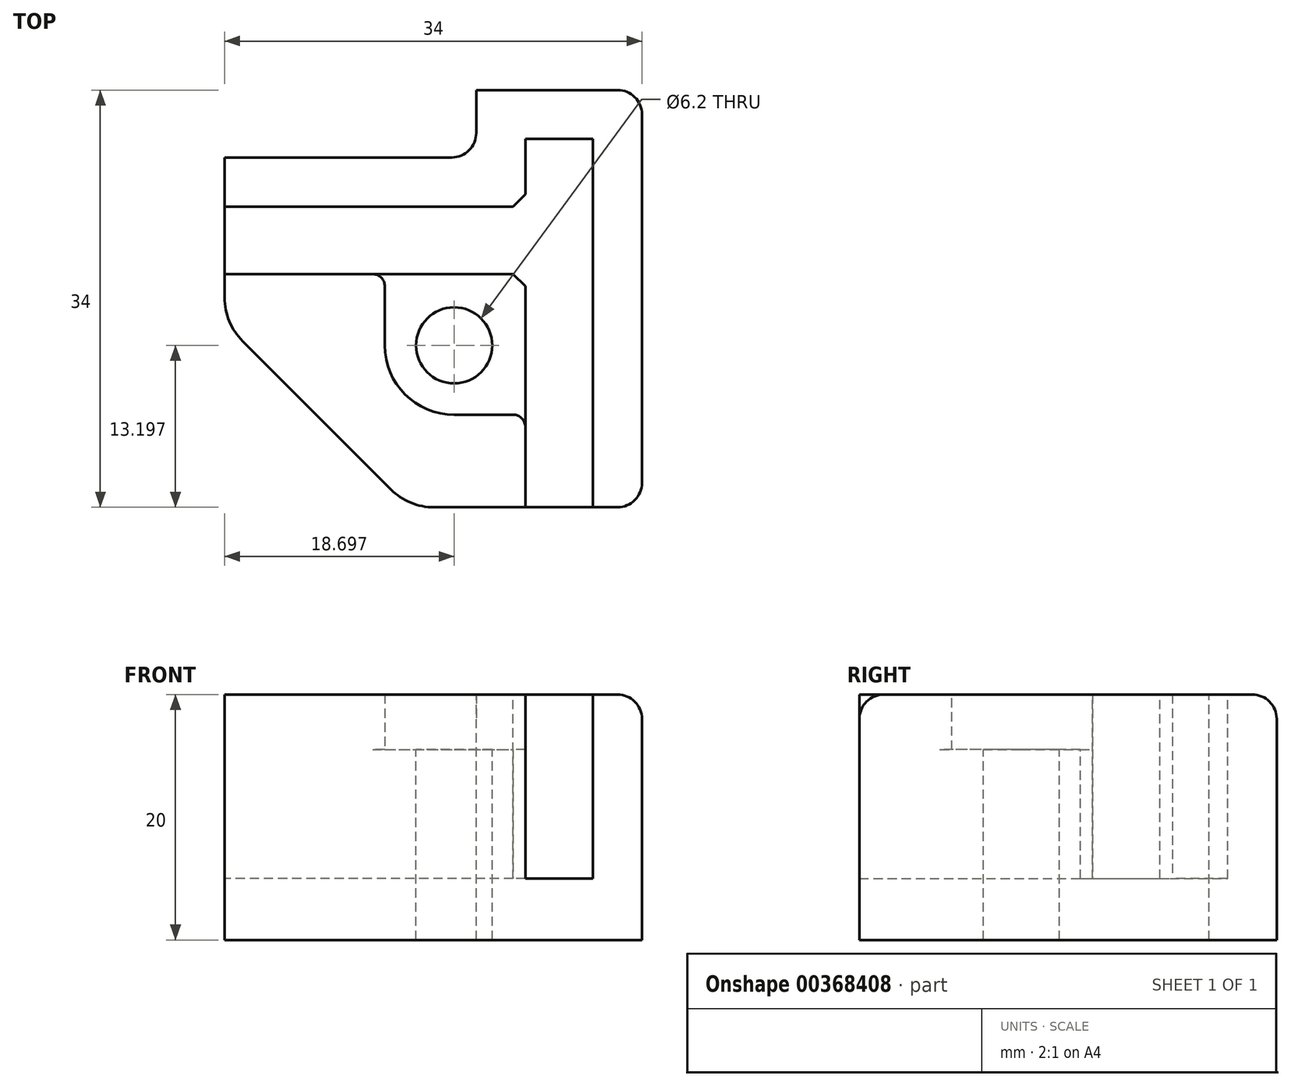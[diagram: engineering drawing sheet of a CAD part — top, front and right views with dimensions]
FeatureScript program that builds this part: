
annotation { "Feature Type Name" : "Feature", "Feature Type Description" : "" }
export const myFeature = defineFeature(function(context is Context, id is Id, definition is map)
    precondition{}
    {
        {
            var Q0;
            Q0=qCreatedBy(makeId("Top.planeOp"),FACE);
            var sketch = newSketch(context, id + "F0", { "sketchPlane" : qUnion([Q0])});
            skLineSegment(sketch, "E0.bottom", {"start": v(0, 0) * mm, "end": v(34, 0) * mm});
            skLineSegment(sketch, "E0.top", {"start": v(0, 34) * mm, "end": v(34, 34) * mm});
            skLineSegment(sketch, "E0.left", {"start": v(0, 0) * mm, "end": v(0, 34) * mm});
            skLineSegment(sketch, "E0.right", {"start": v(34, 0) * mm, "end": v(34, 34) * mm});
            skSolve(sketch);
        }
        {
            var Q0;
            Q0 = qSketchRegion(id + "F0", true);
            extrude(context, id + "F1", {"entities" : qUnion([Q0]), "depth" : 20 * mm});
        }
        {
            var Q0;
            Q0=makeQuery(id+"F1.opExtrude","CAP_FACE",FACE,{"disambiguationData":[OSD([sQuery(id+"F0.wireOp",EDGE,"E0.bottom"),sQuery(id+"F0.wireOp",EDGE,"E0.top"),sQuery(id+"F0.wireOp",EDGE,"E0.left"),sQuery(id+"F0.wireOp",EDGE,"E0.right")])],"isStart":false});
            var sketch = newSketch(context, id + "F2", { "sketchPlane" : qUnion([Q0])});
            skLineSegment(sketch, "E1", {"start": v(30, 0) * mm, "end": v(30, 30) * mm});
            skLineSegment(sketch, "E2", {"start": v(30, 30) * mm, "end": v(24.5, 30) * mm});
            skLineSegment(sketch, "E3", {"start": v(24.5, 30) * mm, "end": v(24.5, 24.5) * mm});
            skLineSegment(sketch, "E4", {"start": v(24.5, 24.5) * mm, "end": v(0, 24.5) * mm});
            skLineSegment(sketch, "E5", {"start": v(30, 0) * mm, "end": v(24.5, 0) * mm});
            skLineSegment(sketch, "E6", {"start": v(24.5, 0) * mm, "end": v(24.5, 19) * mm});
            skLineSegment(sketch, "E7", {"start": v(24.5, 19) * mm, "end": v(0, 19) * mm});
            skLineSegment(sketch, "E8", {"start": v(0, 19) * mm, "end": v(0, 24.5) * mm});
            skSolve(sketch);
        }
        {
            var Q0;
            Q0 = qSketchRegion(id + "F2", true);
            extrude(context, id + "F3", {"entities" : qUnion([Q0]), "operationType" : NewBodyOperationType.REMOVE, "oppositeDirection" : true, "depth" : 15 * mm});
        }
        {
            var Q0;
            Q0=makeQuery(id+"F3.boolean.opBoolean","COPY",EDGE,{"derivedFrom":makeQuery(id+"F3.opExtrude","SWEPT_EDGE",EDGE,{"disambiguationData":[OSD([sQuery(id+"F2.wireOp",EDGE,"E3"),sQuery(id+"F2.wireOp",EDGE,"E4")])]})});
            var Q1;
            Q1=makeQuery(id+"F3.boolean.opBoolean","COPY",EDGE,{"derivedFrom":makeQuery(id+"F3.opExtrude","SWEPT_EDGE",EDGE,{"disambiguationData":[OSD([sQuery(id+"F2.wireOp",EDGE,"E6"),sQuery(id+"F2.wireOp",EDGE,"E7")])]})});
            chamfer(context, id + "F4", {"entities" : qUnion([Q0, Q1]), "width" : 1 * mm, "tangentPropagation" : true});
        }
        {
            var Q0;
            {var subQ0=sQuery(id+"F0.wireOp",EDGE,"E0.bottom");var subQ1=sQuery(id+"F0.wireOp",EDGE,"E0.left");Q0=makeQuery(id+"F3.boolean.opBoolean","SPLIT",FACE,{"disambiguationData":[TD([makeQuery(id+"F3.opExtrude","SWEPT_FACE",FACE,{"disambiguationData":[OSD([sQuery(id+"F2.wireOp",EDGE,"E6")])]})])],"derivedFrom":makeQuery(id+"F1.opExtrude","CAP_FACE",FACE,{"disambiguationData":[OSD([subQ0,sQuery(id+"F0.wireOp",EDGE,"E0.top"),subQ1,sQuery(id+"F0.wireOp",EDGE,"E0.right")])],"isStart":false})});}
            var sketch = newSketch(context, id + "F5", { "sketchPlane" : qUnion([Q0])});
            skLineSegment(sketch, "E9", {"start": v(24, 18.5) * mm, "end": v(18.7, 13.2) * mm, "construction": true});
            skArc(sketch, "E10", {"start": v(13.05, 13.2) * mm, "mid": v(14.7, 9.2) * mm, "end": v(18.7, 7.55) * mm});
            skLineSegment(sketch, "E11", {"start": v(13.05, 13.2) * mm, "end": v(13.05, 20.7) * mm});
            skLineSegment(sketch, "E12", {"start": v(13.05, 20.7) * mm, "end": v(26.05, 20.7) * mm});
            skLineSegment(sketch, "E13", {"start": v(26.05, 20.7) * mm, "end": v(26.05, 7.55) * mm});
            skLineSegment(sketch, "E14", {"start": v(18.7, 7.55) * mm, "end": v(26.05, 7.55) * mm});
            skSolve(sketch);
        }
        {
            var Q0;
            {var subQ0=sQuery(id+"F0.wireOp",EDGE,"E0.left");var subQ1=sQuery(id+"F0.wireOp",EDGE,"E0.top");var subQ2=sQuery(id+"F0.wireOp",EDGE,"E0.right");var subQ3=sQuery(id+"F0.wireOp",EDGE,"E0.bottom");Q0=makeQuery(id+"F3.boolean.opBoolean","SPLIT",FACE,{"disambiguationData":[TD([makeQuery(id+"F1.opExtrude","SWEPT_FACE",FACE,{"disambiguationData":[OSD([subQ1])]})])],"derivedFrom":makeQuery(id+"F1.opExtrude","CAP_FACE",FACE,{"disambiguationData":[OSD([subQ3,subQ1,subQ0,subQ2])],"isStart":false})});}
            var sketch = newSketch(context, id + "F6", { "sketchPlane" : qUnion([Q0])});
            skLineSegment(sketch, "E15.bottom", {"start": v(0, 34) * mm, "end": v(20.5, 34) * mm});
            skLineSegment(sketch, "E15.top", {"start": v(0, 28.5) * mm, "end": v(20.5, 28.5) * mm});
            skLineSegment(sketch, "E15.left", {"start": v(0, 34) * mm, "end": v(0, 28.5) * mm});
            skLineSegment(sketch, "E15.right", {"start": v(20.5, 34) * mm, "end": v(20.5, 28.5) * mm});
            skSolve(sketch);
        }
        {
            var Q0;
            Q0 = qSketchRegion(id + "F6", true);
            extrude(context, id + "F7", {"entities" : qUnion([Q0]), "operationType" : NewBodyOperationType.REMOVE, "endBound" : BoundingType.THROUGH_ALL, "oppositeDirection" : true, "depth" : 25 * mm});
        }
        {
            var Q0;
            Q0=makeQuery(id+"F7.boolean.opBoolean","COPY",EDGE,{"derivedFrom":makeQuery(id+"F7.opExtrude","SWEPT_EDGE",EDGE,{"disambiguationData":[OSD([sQuery(id+"F0.wireOp",EDGE,"E0.left"),sQuery(id+"F6.wireOp",EDGE,"E15.top"),sQuery(id+"F6.wireOp",EDGE,"E15.left")])]})});
            var Q1;
            Q1=makeQuery(id+"F7.boolean.opBoolean","COPY",EDGE,{"derivedFrom":makeQuery(id+"F7.opExtrude","SWEPT_EDGE",EDGE,{"disambiguationData":[OSD([sQuery(id+"F6.wireOp",EDGE,"E15.top"),sQuery(id+"F6.wireOp",EDGE,"E15.right")])]})});
            var Q2;
            Q2=makeQuery(id+"F7.boolean.opBoolean","COPY",EDGE,{"derivedFrom":makeQuery(id+"F7.opExtrude","SWEPT_EDGE",EDGE,{"disambiguationData":[OSD([sQuery(id+"F0.wireOp",EDGE,"E0.top"),sQuery(id+"F6.wireOp",EDGE,"E15.bottom"),sQuery(id+"F6.wireOp",EDGE,"E15.right")])]})});
            var Q3;
            Q3=makeQuery(id+"F1.opExtrude","SWEPT_EDGE",EDGE,{"disambiguationData":[OSD([sQuery(id+"F0.wireOp",EDGE,"E0.top"),sQuery(id+"F0.wireOp",EDGE,"E0.right")])]});
            var Q4;
            Q4=makeQuery(id+"F1.opExtrude","SWEPT_EDGE",EDGE,{"disambiguationData":[OSD([sQuery(id+"F0.wireOp",EDGE,"E0.bottom"),sQuery(id+"F0.wireOp",EDGE,"E0.right")])]});
            fillet(context, id + "F8", {"entities" : qUnion([Q0, Q1, Q2, Q3, Q4]), "radius" : 2 * mm, "tangentPropagation" : true, "allowEdgeOverflow" : false});
        }
        {
            var Q0;
            {var subQ0=sQuery(id+"F0.wireOp",EDGE,"E0.bottom");var subQ1=sQuery(id+"F0.wireOp",EDGE,"E0.right");Q0=makeQuery(id+"F3.boolean.opBoolean","SPLIT",EDGE,{"disambiguationData":[TD([makeQuery(id+"F1.opExtrude","SWEPT_FACE",FACE,{"disambiguationData":[OSD([subQ1])]})])],"derivedFrom":makeQuery(id+"F1.opExtrude","CAP_EDGE",EDGE,{"disambiguationData":[OSD([subQ0])],"isStart":false})});}
            fillet(context, id + "F9", {"entities" : qUnion([Q0]), "radius" : 2 * mm, "tangentPropagation" : true, "allowEdgeOverflow" : false});
        }
        {
            var Q0;
            Q0 = qSketchRegion(id + "F5", true);
            extrude(context, id + "F10", {"entities" : qUnion([Q0]), "operationType" : NewBodyOperationType.REMOVE, "oppositeDirection" : true, "depth" : 4.5 * mm});
        }
        {
            var Q0;
            Q0=makeQuery(id+"F10.boolean.opBoolean","COPY",FACE,{"derivedFrom":makeQuery(id+"F10.opExtrude","CAP_FACE",FACE,{"disambiguationData":[OSD([sQuery(id+"F5.wireOp",EDGE,"E10")])],"isStart":false})});
            var sketch = newSketch(context, id + "F11", { "sketchPlane" : qUnion([Q0])});
            skCircle(sketch, "E16", {"center": v(18.7, 13.2) * mm, "radius": 3.1 * mm});
            skSolve(sketch);
        }
        {
            var Q0;
            Q0 = qSketchRegion(id + "F11", true);
            extrude(context, id + "F12", {"entities" : qUnion([Q0]), "operationType" : NewBodyOperationType.REMOVE, "endBound" : BoundingType.THROUGH_ALL, "oppositeDirection" : true, "depth" : 25 * mm});
        }
        {
            var Q0;
            Q0=makeQuery(id+"F10.boolean.opBoolean","INTERSECT",EDGE,{"derivedFrom":[makeQuery(id+"F3.boolean.opBoolean","COPY",FACE,{"derivedFrom":makeQuery(id+"F3.opExtrude","SWEPT_FACE",FACE,{"disambiguationData":[OSD([sQuery(id+"F2.wireOp",EDGE,"E7")])]})}),makeQuery(id+"F10.opExtrude","SWEPT_FACE",FACE,{"disambiguationData":[OSD([sQuery(id+"F5.wireOp",EDGE,"E11")])]})]});
            var Q1;
            Q1=makeQuery(id+"F10.boolean.opBoolean","INTERSECT",EDGE,{"derivedFrom":[makeQuery(id+"F3.boolean.opBoolean","COPY",FACE,{"derivedFrom":makeQuery(id+"F3.opExtrude","SWEPT_FACE",FACE,{"disambiguationData":[OSD([sQuery(id+"F2.wireOp",EDGE,"E6")])]})}),makeQuery(id+"F10.opExtrude","SWEPT_FACE",FACE,{"disambiguationData":[OSD([sQuery(id+"F5.wireOp",EDGE,"E14")])]})]});
            fillet(context, id + "F13", {"entities" : qUnion([Q0, Q1]), "radius" : 1 * mm, "tangentPropagation" : true, "allowEdgeOverflow" : false});
        }
        {
            var Q0;
            Q0=makeQuery(id+"F1.opExtrude","SWEPT_EDGE",EDGE,{"disambiguationData":[OSD([sQuery(id+"F0.wireOp",EDGE,"E0.bottom"),sQuery(id+"F0.wireOp",EDGE,"E0.left")])]});
            chamfer(context, id + "F14", {"entities" : qUnion([Q0]), "width" : 15 * mm, "tangentPropagation" : true});
        }
        {
            var Q0;
            {var subQ0=sQuery(id+"F0.wireOp",EDGE,"E0.left");Q0=makeQuery(id+"F14.opChamfer","BLEND_EDGE",EDGE,{"blendedFrom":[makeQuery(id+"F1.opExtrude","SWEPT_EDGE",EDGE,{"disambiguationData":[OSD([sQuery(id+"F0.wireOp",EDGE,"E0.bottom"),subQ0])]}),makeQuery(id+"F1.opExtrude","SWEPT_FACE",FACE,{"disambiguationData":[OSD([subQ0])]})],"blendedInto":[makeQuery(id+"F1.opExtrude","SWEPT_FACE",FACE,{"disambiguationData":[OSD([subQ0])]})]});}
            var Q1;
            {var subQ0=sQuery(id+"F0.wireOp",EDGE,"E0.bottom");Q1=makeQuery(id+"F14.opChamfer","BLEND_EDGE",EDGE,{"blendedFrom":[makeQuery(id+"F1.opExtrude","SWEPT_EDGE",EDGE,{"disambiguationData":[OSD([subQ0,sQuery(id+"F0.wireOp",EDGE,"E0.left")])]}),makeQuery(id+"F1.opExtrude","SWEPT_FACE",FACE,{"disambiguationData":[OSD([subQ0])]})],"blendedInto":[makeQuery(id+"F1.opExtrude","SWEPT_FACE",FACE,{"disambiguationData":[OSD([subQ0])]})]});}
            fillet(context, id + "F15", {"entities" : qUnion([Q0, Q1]), "radius" : 5 * mm, "tangentPropagation" : true, "allowEdgeOverflow" : false});
        }
    });
